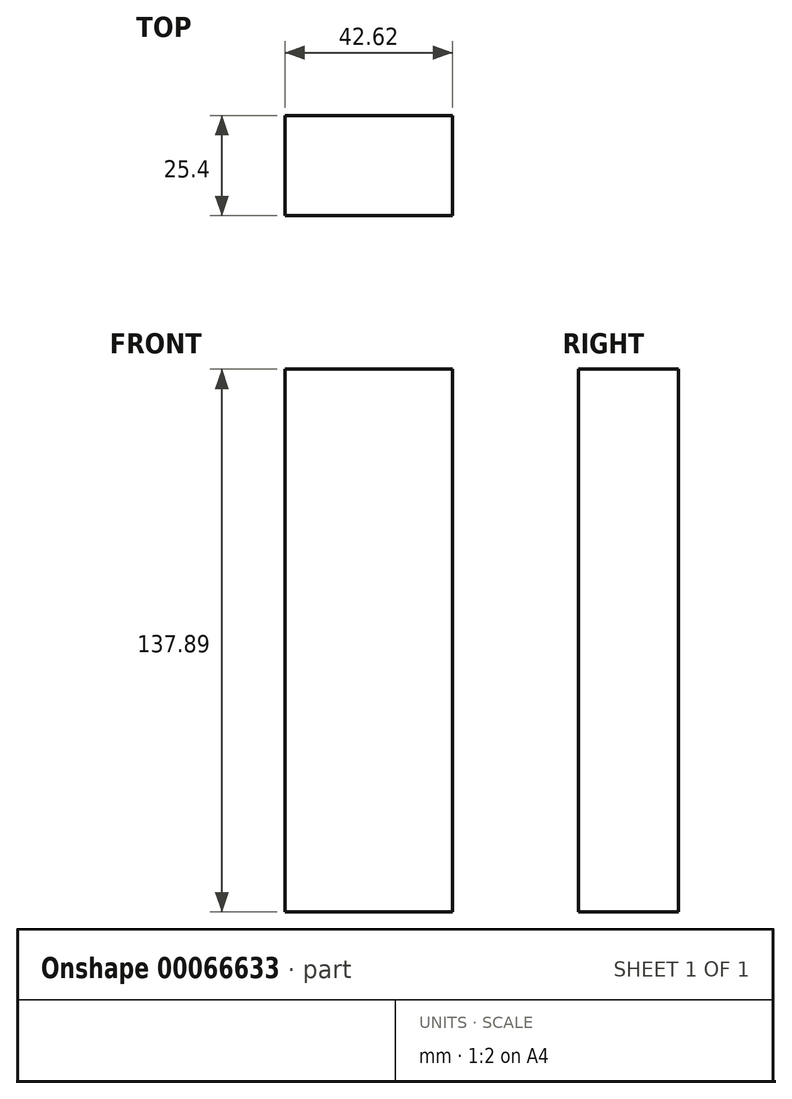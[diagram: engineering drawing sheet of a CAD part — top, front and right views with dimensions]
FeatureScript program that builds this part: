
annotation { "Feature Type Name" : "Feature", "Feature Type Description" : "" }
export const myFeature = defineFeature(function(context is Context, id is Id, definition is map)
    precondition{}
    {
        {
            var Q0;
            Q0=qCreatedBy(makeId("Front.planeOp"),FACE);
            var sketch = newSketch(context, id + "F0", { "sketchPlane" : qUnion([Q0])});
            skLineSegment(sketch, "E0.bottom", {"start": v(-42.78, 106.19) * mm, "end": v(-0.16, 106.19) * mm});
            skLineSegment(sketch, "E0.top", {"start": v(-42.78, -31.7) * mm, "end": v(-0.16, -31.7) * mm});
            skLineSegment(sketch, "E0.left", {"start": v(-42.78, 106.19) * mm, "end": v(-42.78, -31.7) * mm});
            skLineSegment(sketch, "E0.right", {"start": v(-0.16, 106.19) * mm, "end": v(-0.16, -31.7) * mm});
            skSolve(sketch);
        }
        {
            var Q0;
            Q0 = qSketchRegion(id + "F0", true);
            var Q1;
            Q1=makeQuery(id+"F0.imprint","IMPRINT",FACE,{"disambiguationData":[TD([[makeQuery(id+"F0.imprint","IMPRINT",EDGE,{"derivedFrom":sQuery(id+"F0.wireOp",EDGE,"E0.bottom")}),-1.0]])]});
            extrude(context, id + "F1", {"entities" : qUnion([Q0, Q1]), "depth" : 25.4 * mm});
        }
    });
